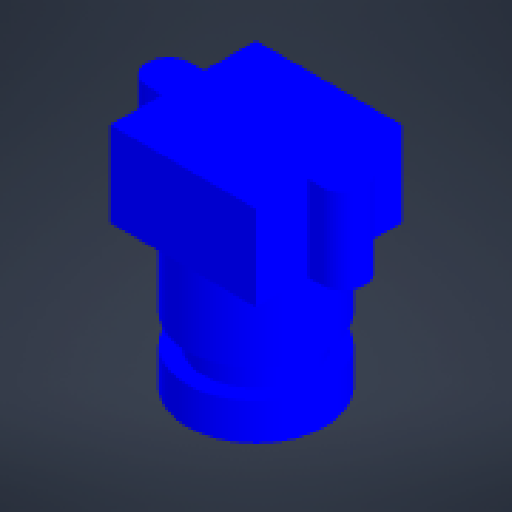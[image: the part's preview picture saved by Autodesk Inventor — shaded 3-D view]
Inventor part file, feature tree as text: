
AUTODESK INVENTOR PART (.ipt)
format: ipt  version: 2024 (Build 280153000, 153)  size: 229,376 bytes
history: native  units: mm
features: extrude x4, sketch x4, other x1
ambient origin geometry x8: Origin, YZ Plane, XZ Plane, XY Plane, X Axis, Y Axis, Z Axis, Center Point
bodies: Body1 (feature_tree)
feature tree (9):
  other  "Твердое тело1"
  extrude  "Выдавливание1"  Depth=4.7mm
  extrude  "Выдавливание2"  Depth=4.0mm
  extrude  "Выдавливание3"  Depth=16.3mm
  extrude  "Выдавливание4"  Depth=16.3mm
  sketch  "Эскиз1"
  sketch  "Эскиз2"
  sketch  "Эскиз3"
  sketch  "Эскиз4"
